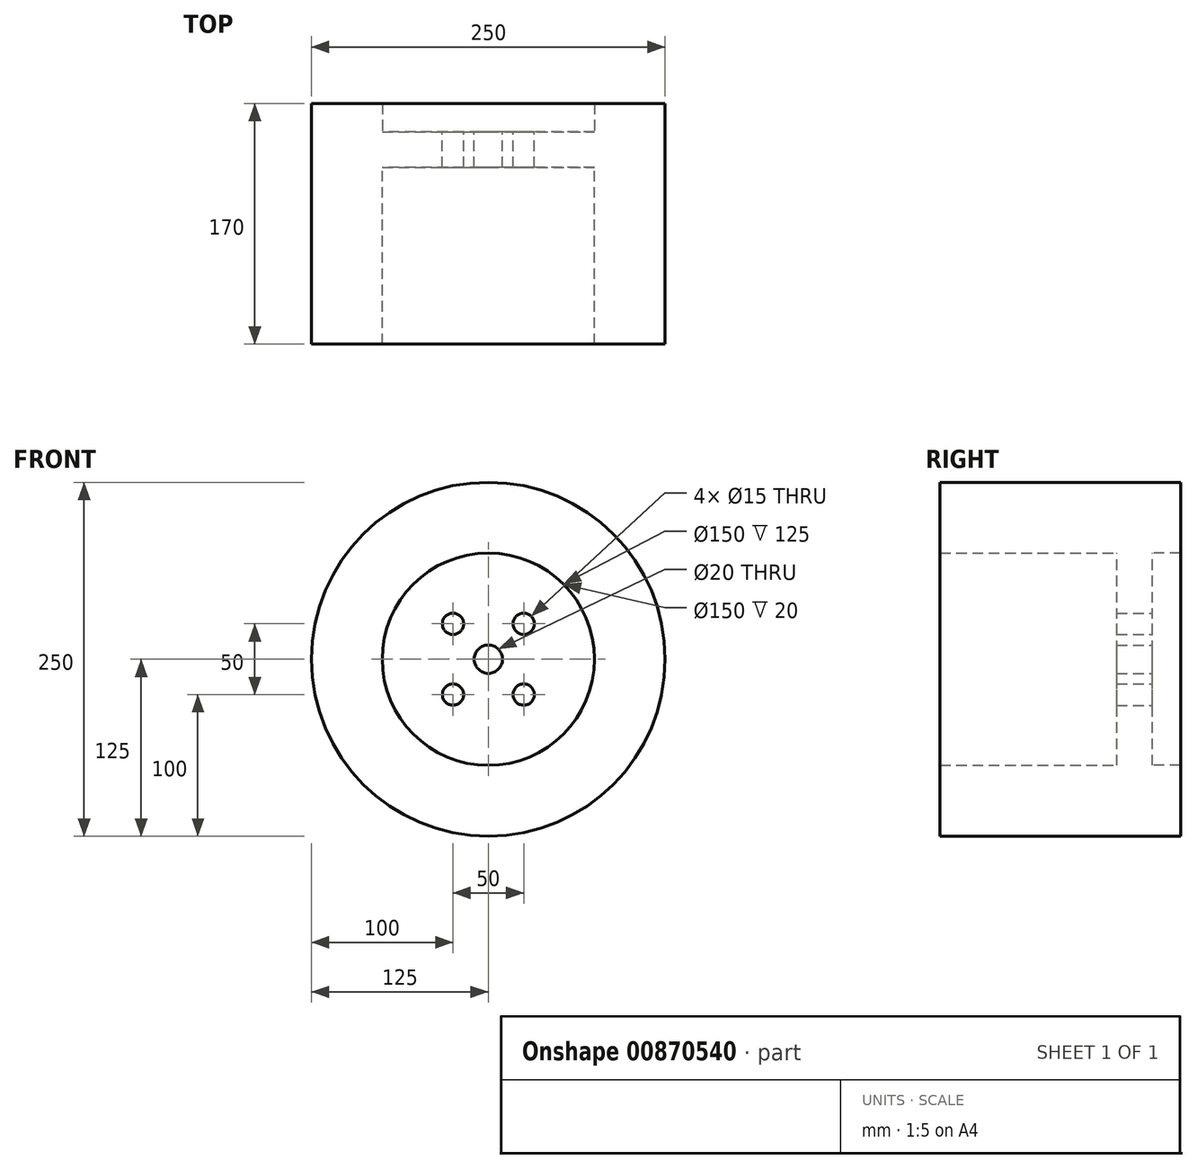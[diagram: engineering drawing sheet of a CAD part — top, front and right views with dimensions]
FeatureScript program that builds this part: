
annotation { "Feature Type Name" : "Feature", "Feature Type Description" : "" }
export const myFeature = defineFeature(function(context is Context, id is Id, definition is map)
    precondition{}
    {
        {
            var Q0;
            Q0=qCreatedBy(makeId("Front.planeOp"),FACE);
            var sketch = newSketch(context, id + "F0", { "sketchPlane" : qUnion([Q0])});
            skCircle(sketch, "E0", {"center": v(0, 0) * mm, "radius": 75 * mm});
            skCircle(sketch, "E1", {"center": v(0, 0) * mm, "radius": 125 * mm});
            skCircle(sketch, "E2", {"center": v(-25, 25) * mm, "radius": 7.5 * mm});
            skCircle(sketch, "E3", {"center": v(25, 25) * mm, "radius": 7.5 * mm});
            skCircle(sketch, "E4", {"center": v(25, -25) * mm, "radius": 7.5 * mm});
            skCircle(sketch, "E5", {"center": v(-25, -25) * mm, "radius": 7.5 * mm});
            skCircle(sketch, "E6", {"center": v(0, 0) * mm, "radius": 10 * mm});
            skSolve(sketch);
        }
        {
            var Q0;
            Q0 = qSketchRegion(id + "F0", true);
            extrude(context, id + "F1", {"entities" : qUnion([Q0]), "depth" : 150 * mm, "offsetDistance" : 25 * mm});
        }
        {
            var Q0;
            Q0=makeQuery(id+"F0.imprint","IMPRINT",FACE,{"disambiguationData":[TD([[makeQuery(id+"F0.imprint","IMPRINT",EDGE,{"derivedFrom":sQuery(id+"F0.wireOp",EDGE,"E0")}),1.0]])]});
            extrude(context, id + "F2", {"entities" : qUnion([Q0]), "depth" : 25 * mm, "offsetDistance" : 25 * mm});
        }
        {
            var Q0;
            Q0=makeQuery(id+"F0.imprint","IMPRINT",FACE,{"disambiguationData":[TD([[makeQuery(id+"F0.imprint","IMPRINT",EDGE,{"derivedFrom":sQuery(id+"F0.wireOp",EDGE,"E0")}),-1.0]])]});
            extrude(context, id + "F3", {"entities" : qUnion([Q0]), "operationType" : NewBodyOperationType.ADD, "depth" : 150 * mm, "offsetDistance" : 25 * mm});
        }
        {
            var Q0;
            Q0=makeQuery(id+"F0.imprint","IMPRINT",FACE,{"disambiguationData":[TD([[makeQuery(id+"F0.imprint","IMPRINT",EDGE,{"derivedFrom":sQuery(id+"F0.wireOp",EDGE,"E0")}),-1.0]])]});
            extrude(context, id + "F4", {"entities" : qUnion([Q0]), "operationType" : NewBodyOperationType.ADD, "depth" : -20 * mm, "offsetDistance" : 25 * mm});
        }
    });
